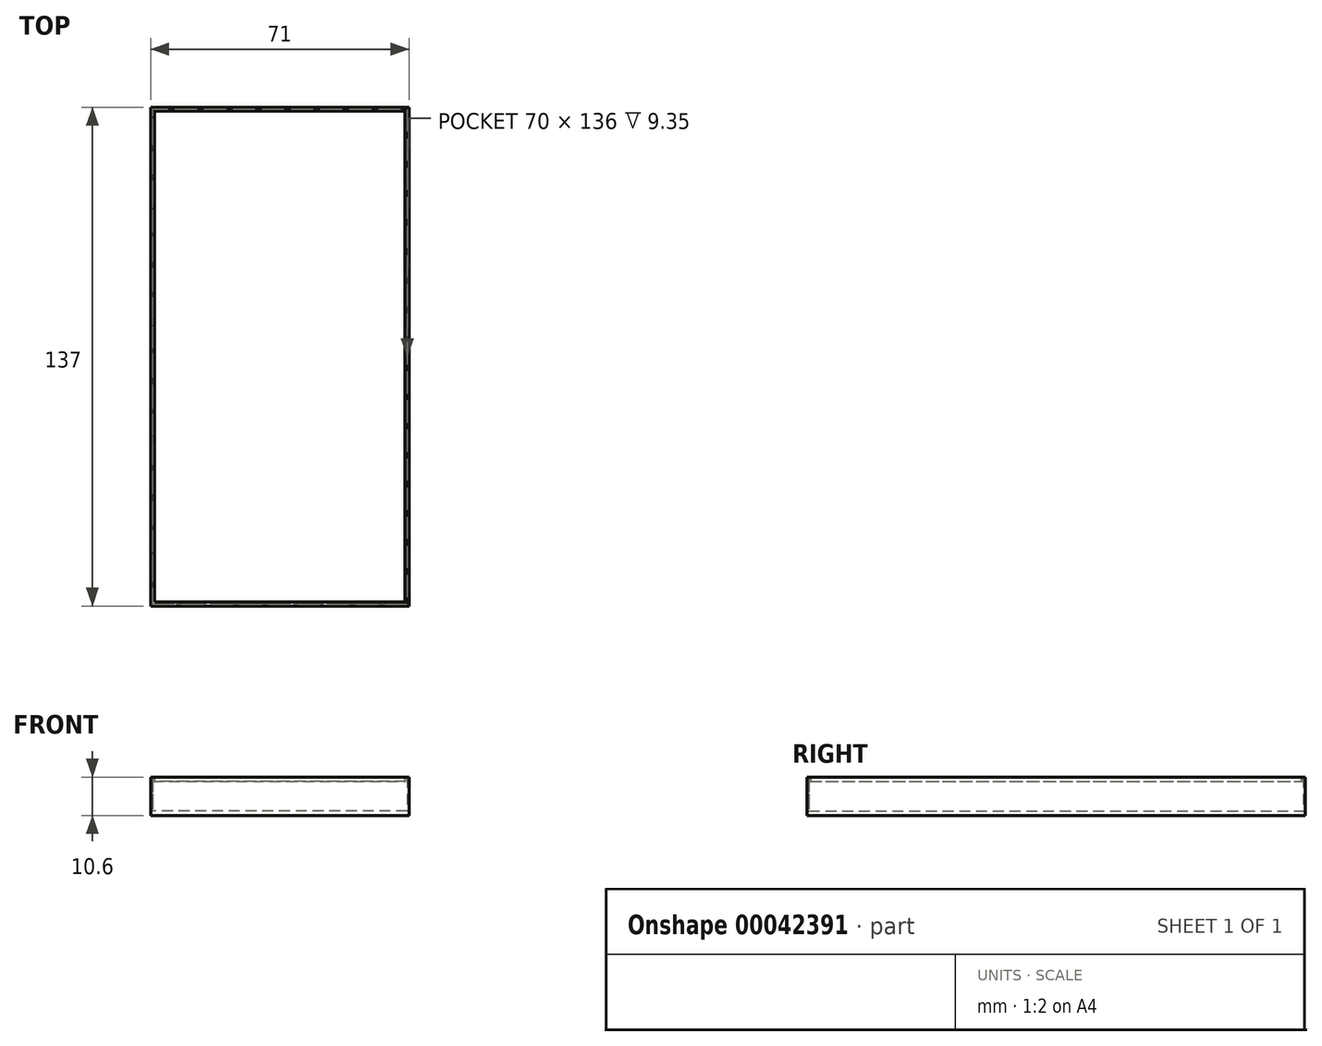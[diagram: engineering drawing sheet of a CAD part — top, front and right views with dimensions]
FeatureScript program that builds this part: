
annotation { "Feature Type Name" : "Feature", "Feature Type Description" : "" }
export const myFeature = defineFeature(function(context is Context, id is Id, definition is map)
    precondition{}
    {
        {
            var Q0;
            Q0=qCreatedBy(makeId("Top.planeOp"),FACE);
            var sketch = newSketch(context, id + "F0", { "sketchPlane" : qUnion([Q0])});
            skLineSegment(sketch, "E0.rect.bottom", {"start": v(-35.5, 66.77) * mm, "end": v(35.5, 66.77) * mm});
            skLineSegment(sketch, "E0.rect.top", {"start": v(-35.5, -70.23) * mm, "end": v(35.5, -70.23) * mm});
            skLineSegment(sketch, "E0.rect.left", {"start": v(-35.5, 66.77) * mm, "end": v(-35.5, -70.23) * mm});
            skLineSegment(sketch, "E0.rect.right", {"start": v(35.5, 66.77) * mm, "end": v(35.5, -70.23) * mm});
            skPoint(sketch, "E0.rect.middle", {"position": v(0, -1.73) * mm});
            skSolve(sketch);
        }
        {
            var Q0;
            Q0 = qSketchRegion(id + "F0", true);
            extrude(context, id + "F1", {"entities" : qUnion([Q0]), "depth" : 1.25 * mm});
        }
        {
            var Q0;
            Q0=makeQuery(id+"F1.opExtrude","CAP_FACE",FACE,{"disambiguationData":[OSD([sQuery(id+"F0.wireOp",EDGE,"E0.rect.bottom"),sQuery(id+"F0.wireOp",EDGE,"E0.rect.top"),sQuery(id+"F0.wireOp",EDGE,"E0.rect.left"),sQuery(id+"F0.wireOp",EDGE,"E0.rect.right")])],"isStart":false});
            var sketch = newSketch(context, id + "F2", { "sketchPlane" : qUnion([Q0])});
            skLineSegment(sketch, "E1.bottom", {"start": v(-35.5, 66.77) * mm, "end": v(-35, 66.77) * mm});
            skLineSegment(sketch, "E1.top", {"start": v(-35.5, 66.27) * mm, "end": v(-35, 66.27) * mm});
            skLineSegment(sketch, "E1.left", {"start": v(-35.5, 66.77) * mm, "end": v(-35.5, 66.27) * mm});
            skLineSegment(sketch, "E1.right", {"start": v(-35, 66.77) * mm, "end": v(-35, 66.27) * mm});
            skLineSegment(sketch, "E2.bottom", {"start": v(35.5, -70.23) * mm, "end": v(35, -70.23) * mm});
            skLineSegment(sketch, "E2.top", {"start": v(35.5, -69.73) * mm, "end": v(35, -69.73) * mm});
            skLineSegment(sketch, "E2.left", {"start": v(35.5, -70.23) * mm, "end": v(35.5, -69.73) * mm});
            skLineSegment(sketch, "E2.right", {"start": v(35, -70.23) * mm, "end": v(35, -69.73) * mm});
            skLineSegment(sketch, "E3.bottom", {"start": v(35, -69.73) * mm, "end": v(-35, -69.73) * mm});
            skLineSegment(sketch, "E3.top", {"start": v(35, 66.27) * mm, "end": v(-35, 66.27) * mm});
            skLineSegment(sketch, "E3.left", {"start": v(35, -69.73) * mm, "end": v(35, 66.27) * mm});
            skLineSegment(sketch, "E3.right", {"start": v(-35, -69.73) * mm, "end": v(-35, 66.27) * mm});
            skSolve(sketch);
        }
        {
            var Q0;
            Q0=makeQuery(id+"F2.imprint","IMPRINT",FACE,{"disambiguationData":[TD([[makeQuery(id+"F2.imprint","IMPRINT",EDGE,{"derivedFrom":sQuery(id+"F2.wireOp",EDGE,"E1.bottom")}),-1.0]])]});
            var Q1;
            Q1=makeQuery(id+"F2.imprint","IMPRINT",FACE,{"disambiguationData":[TD([[makeQuery(id+"F2.imprint","IMPRINT",EDGE,{"derivedFrom":sQuery(id+"F2.wireOp",EDGE,"E2.bottom")}),1.0]])]});
            var Q2;
            {var subQ4=sQuery(id+"F2.wireOp",EDGE,"E1.top");Q2=makeQuery(id+"F2.imprint","IMPRINT",FACE,{"disambiguationData":[TD([[makeQuery(id+"F2.imprint","IMPRINT",EDGE,{"derivedFrom":subQ4}),-1.0]])]});}
            var Q3;
            {var subQ4=sQuery(id+"F2.wireOp",EDGE,"E1.right");Q3=makeQuery(id+"F2.imprint","IMPRINT",FACE,{"disambiguationData":[TD([[makeQuery(id+"F2.imprint","IMPRINT",EDGE,{"derivedFrom":subQ4}),1.0]])]});}
            extrude(context, id + "F3", {"entities" : qUnion([Q0, Q1, Q2, Q3]), "operationType" : NewBodyOperationType.ADD, "depth" : 8.1 * mm});
        }
        {
            var Q0;
            Q0=makeQuery(id+"F3.opExtrude","CAP_FACE",FACE,{"disambiguationData":[OSD([sQuery(id+"F0.wireOp",EDGE,"E0.rect.bottom"),sQuery(id+"F0.wireOp",EDGE,"E0.rect.top"),sQuery(id+"F0.wireOp",EDGE,"E0.rect.left"),sQuery(id+"F0.wireOp",EDGE,"E0.rect.right"),sQuery(id+"F2.wireOp",EDGE,"E1.bottom"),sQuery(id+"F2.wireOp",EDGE,"E1.left"),sQuery(id+"F2.wireOp",EDGE,"E2.bottom"),sQuery(id+"F2.wireOp",EDGE,"E2.left"),sQuery(id+"F2.wireOp",EDGE,"E3.bottom"),sQuery(id+"F2.wireOp",EDGE,"E3.top"),sQuery(id+"F2.wireOp",EDGE,"E3.left"),sQuery(id+"F2.wireOp",EDGE,"E3.right")])],"isStart":false});
            var sketch = newSketch(context, id + "F4", { "sketchPlane" : qUnion([Q0])});
            skLineSegment(sketch, "E4.bottom", {"start": v(-35, 66.27) * mm, "end": v(-34.4, 66.27) * mm});
            skLineSegment(sketch, "E4.top", {"start": v(-35, 65.67) * mm, "end": v(-34.4, 65.67) * mm});
            skLineSegment(sketch, "E4.left", {"start": v(-35, 66.27) * mm, "end": v(-35, 65.67) * mm});
            skLineSegment(sketch, "E4.right", {"start": v(-34.4, 66.27) * mm, "end": v(-34.4, 65.67) * mm});
            skLineSegment(sketch, "E5.bottom", {"start": v(-35.5, 66.77) * mm, "end": v(35.5, 66.77) * mm});
            skLineSegment(sketch, "E5.top", {"start": v(-35.5, -70.23) * mm, "end": v(35.5, -70.23) * mm});
            skLineSegment(sketch, "E5.left", {"start": v(-35.5, 66.77) * mm, "end": v(-35.5, -70.23) * mm});
            skLineSegment(sketch, "E5.right", {"start": v(35.5, 66.77) * mm, "end": v(35.5, -70.23) * mm});
            skLineSegment(sketch, "E6.bottom", {"start": v(35, -69.73) * mm, "end": v(34.4, -69.73) * mm});
            skLineSegment(sketch, "E6.top", {"start": v(35, -69.13) * mm, "end": v(34.4, -69.13) * mm});
            skLineSegment(sketch, "E6.left", {"start": v(35, -69.73) * mm, "end": v(35, -69.13) * mm});
            skLineSegment(sketch, "E6.right", {"start": v(34.4, -69.73) * mm, "end": v(34.4, -69.13) * mm});
            skLineSegment(sketch, "E7.bottom", {"start": v(34.4, -69.13) * mm, "end": v(-34.4, -69.13) * mm});
            skLineSegment(sketch, "E7.top", {"start": v(34.4, 65.67) * mm, "end": v(-34.4, 65.67) * mm});
            skLineSegment(sketch, "E7.left", {"start": v(34.4, -69.13) * mm, "end": v(34.4, 65.67) * mm});
            skLineSegment(sketch, "E7.right", {"start": v(-34.4, -69.13) * mm, "end": v(-34.4, 65.67) * mm});
            skSolve(sketch);
        }
        {
            var Q0;
            {var subQ9=sQuery(id+"F4.wireOp",EDGE,"E4.bottom");Q0=makeQuery(id+"F4.imprint","IMPRINT",FACE,{"disambiguationData":[TD([[makeQuery(id+"F4.imprint","IMPRINT",EDGE,{"derivedFrom":subQ9}),-1.0]])]});}
            var Q1;
            {var subQ1=sQuery(id+"F4.wireOp",EDGE,"E4.top");Q1=makeQuery(id+"F4.imprint","IMPRINT",FACE,{"disambiguationData":[TD([[makeQuery(id+"F4.imprint","IMPRINT",EDGE,{"derivedFrom":subQ1}),-1.0]])]});}
            extrude(context, id + "F5", {"entities" : qUnion([Q0, Q1]), "operationType" : NewBodyOperationType.ADD, "depth" : 1.25 * mm});
        }
        {
            var Q0;
            Q0=makeQuery(id+"F5.opExtrude","CAP_FACE",FACE,{"disambiguationData":[OSD([sQuery(id+"F2.wireOp",EDGE,"E3.top"),sQuery(id+"F2.wireOp",EDGE,"E3.left"),sQuery(id+"F4.wireOp",EDGE,"E4.bottom"),sQuery(id+"F4.wireOp",EDGE,"E4.top"),sQuery(id+"F4.wireOp",EDGE,"E4.left"),sQuery(id+"F4.wireOp",EDGE,"E5.bottom"),sQuery(id+"F4.wireOp",EDGE,"E5.top"),sQuery(id+"F4.wireOp",EDGE,"E5.left"),sQuery(id+"F4.wireOp",EDGE,"E5.right"),sQuery(id+"F4.wireOp",EDGE,"E6.bottom"),sQuery(id+"F4.wireOp",EDGE,"E6.left"),sQuery(id+"F4.wireOp",EDGE,"E6.right"),sQuery(id+"F4.wireOp",EDGE,"E7.bottom"),sQuery(id+"F4.wireOp",EDGE,"E7.right")])],"isStart":false});
            var sketch = newSketch(context, id + "F6", { "sketchPlane" : qUnion([Q0])});
            skLineSegment(sketch, "E8.bottom", {"start": v(-35, 66.27) * mm, "end": v(35, 66.27) * mm});
            skLineSegment(sketch, "E8.top", {"start": v(-35, 65.67) * mm, "end": v(35, 65.67) * mm});
            skLineSegment(sketch, "E8.left", {"start": v(-35, 66.27) * mm, "end": v(-35, 65.67) * mm});
            skLineSegment(sketch, "E8.right", {"start": v(35, 66.27) * mm, "end": v(35, 65.67) * mm});
            skLineSegment(sketch, "E9.bottom", {"start": v(34.4, -69.73) * mm, "end": v(35, -69.73) * mm});
            skLineSegment(sketch, "E9.top", {"start": v(34.4, 66.27) * mm, "end": v(35, 66.27) * mm});
            skLineSegment(sketch, "E9.left", {"start": v(34.4, -69.73) * mm, "end": v(34.4, 66.27) * mm});
            skLineSegment(sketch, "E9.right", {"start": v(35, -69.73) * mm, "end": v(35, 66.27) * mm});
            skSolve(sketch);
        }
        {
            var Q0;
            Q0 = qSketchRegion(id + "F6", true);
            extrude(context, id + "F7", {"entities" : qUnion([Q0]), "oppositeDirection" : true, "depth" : 1.25 * mm});
        }
    });
